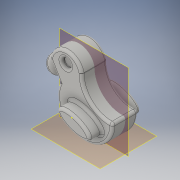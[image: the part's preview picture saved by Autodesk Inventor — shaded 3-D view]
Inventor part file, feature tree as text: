
AUTODESK INVENTOR PART (.ipt)
format: ipt  version: 2016 (Build 200138000, 138)  size: 414,720 bytes
history: native  units: in
note: dims shown in document units (in); Inventor stores cm internally (conversion verified against a paired STEP export)
features: sketch x10, extrude x6, fillet x4, plane x3, mirror x2, other x1
ambient origin geometry x8: Origin, YZ Plane, XZ Plane, XY Plane, X Axis, Y Axis, Z Axis, Center Point
bodies: Solid1 (feature_tree)
feature tree (26):
  extrude  "Extrusion1"  Depth=0.15in TaperAngle=0.0deg
  extrude  "Extrusion3"  Depth=0.0394in TaperAngle=0.0deg
  sketch  "Sketch7"  dims[d6=0.1in d7=0.0in d9=0.0394in d10=0.0in]
  sketch  "Sketch9"  dims[d12=0.1575in d13=0.0687in d14=0.1969in d15=0.0206in]
  sketch  "Sketch10"  dims[d16=0.03in d17=0.03in]
  plane  "Work Plane8"
  mirror  "Mirror6"
  plane  "Work Plane9"
  extrude  "Extrusion4"  Depth=0.1969in
  extrude  "Extrusion5"  Depth=0.03in
  mirror  "Mirror7"
  sketch  "Sketch17"
  extrude  "Extrusion6"  Depth=0.03in
  sketch  "Sketch19"
  sketch  "Sketch20"
  extrude  "Extrusion7"  [1 undecoded]
  fillet  "Fillet2"  [1 undecoded]
  fillet  "Fillet3"  [1 undecoded]
  fillet  "Fillet4"  [1 undecoded]
  fillet  "Fillet5"  [1 undecoded]
  other  "Duck"
  sketch  "Sketch6"  dims[d0=0.3in d1=0.0in d4=0.15in d5=0.0in]
  sketch  "Sketch11"  dims[d18=0.03in d19=0.03in]
  sketch  "Sketch15"
  plane  "Work Plane10"
  sketch  "Sketch18"
note: 5 required parameter values undecoded (feature->parameter linkage not recoverable at this tier; creation-order binding heuristic only, values carry confidence <= 0.55)
